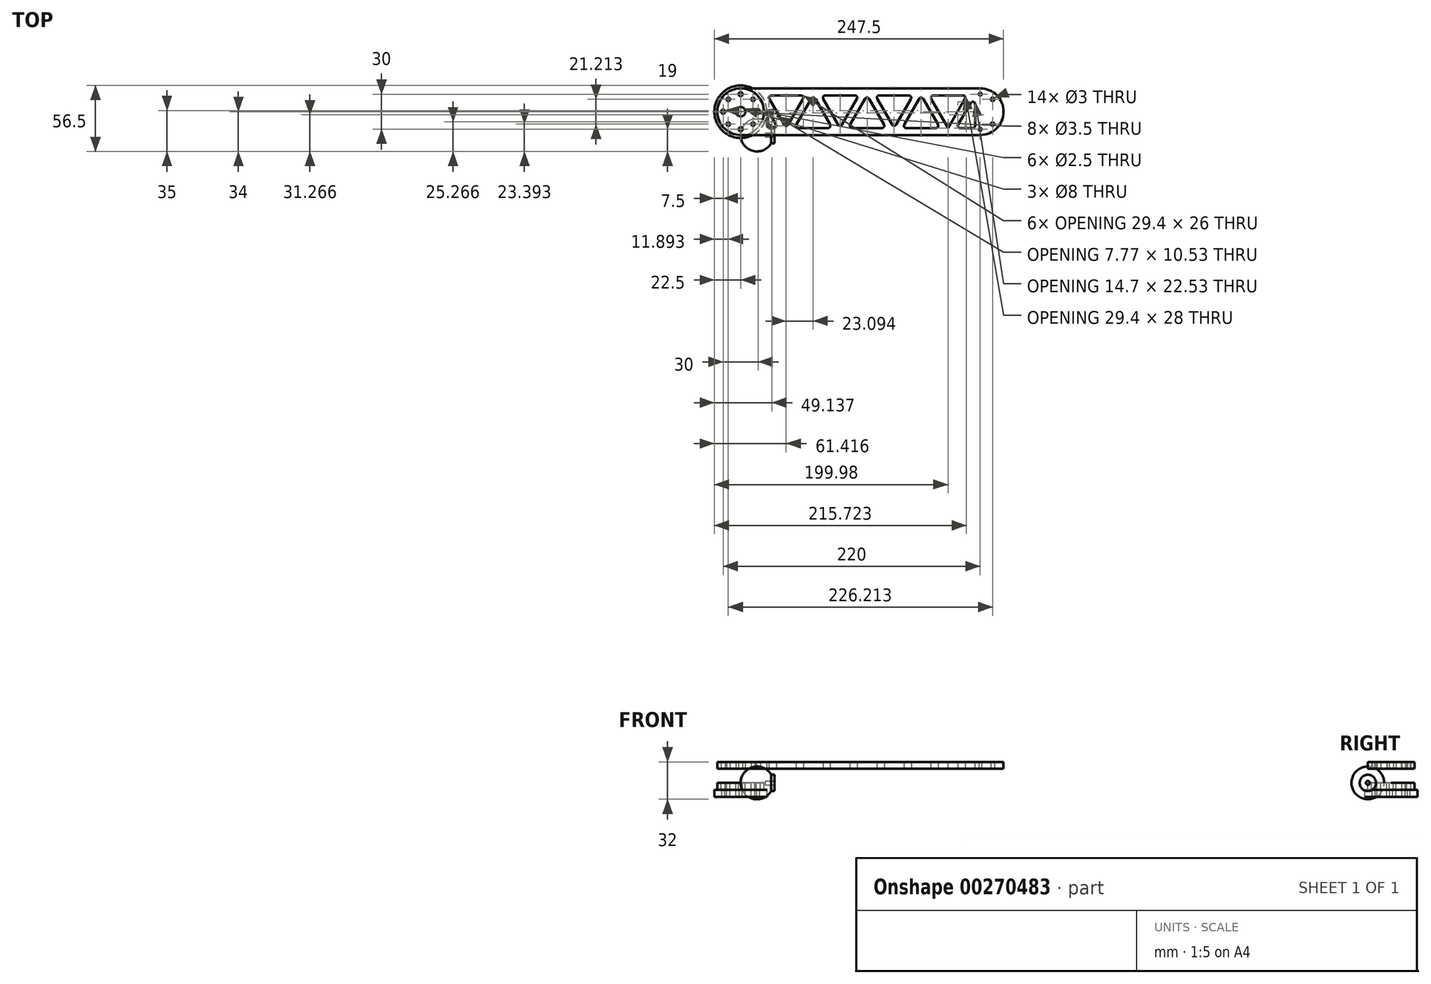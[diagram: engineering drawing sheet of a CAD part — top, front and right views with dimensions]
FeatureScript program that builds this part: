
annotation { "Feature Type Name" : "Feature", "Feature Type Description" : "" }
export const myFeature = defineFeature(function(context is Context, id is Id, definition is map)
    precondition{}
    {
        {
            var Q0;
            Q0=qCreatedBy(makeId("Top.planeOp"),FACE);
            var sketch = newSketch(context, id + "F0", { "sketchPlane" : qUnion([Q0])});
            skLineSegment(sketch, "E0.bottom", {"start": v(0, 0) * mm, "end": v(205, 0) * mm});
            skLineSegment(sketch, "E0.top", {"start": v(0, 40) * mm, "end": v(205, 40) * mm});
            skArc(sketch, "E1", {"start": v(205, 40) * mm, "mid": v(225, 20) * mm, "end": v(205, 0) * mm});
            skArc(sketch, "E2", {"start": v(0, 40) * mm, "mid": v(-20, 20) * mm, "end": v(0, 0) * mm});
            skCircle(sketch, "E3", {"center": v(0, 20) * mm, "radius": 15 * mm, "construction": true});
            skCircle(sketch, "E4", {"center": v(0, 35) * mm, "radius": 1.75 * mm});
            skCircle(sketch, "E5.1.0", {"center": v(-15, 20) * mm, "radius": 1.75 * mm});
            skCircle(sketch, "E5.2.0", {"center": v(0, 5) * mm, "radius": 1.75 * mm});
            skCircle(sketch, "E5.3.0", {"center": v(15, 20) * mm, "radius": 1.75 * mm});
            skLineSegment(sketch, "E6", {"start": v(0, 20) * mm, "end": v(10.6, 30.6) * mm});
            skCircle(sketch, "E7", {"center": v(10.6, 30.6) * mm, "radius": 1.5 * mm});
            skCircle(sketch, "E8.1.0", {"center": v(-10.6, 30.6) * mm, "radius": 1.5 * mm});
            skCircle(sketch, "E8.2.0", {"center": v(-10.6, 9.4) * mm, "radius": 1.5 * mm});
            skCircle(sketch, "E8.3.0", {"center": v(10.6, 9.4) * mm, "radius": 1.5 * mm});
            skCircle(sketch, "E9", {"center": v(0, 20) * mm, "radius": 4 * mm});
            skLineSegment(sketch, "E10", {"start": v(102.5, 40) * mm, "end": v(102.5, 0) * mm, "construction": true});
            skCircle(sketch, "E11.MirrorC", {"center": v(215.6, 30.6) * mm, "radius": 1.5 * mm});
            skCircle(sketch, "E12.MirrorC", {"center": v(215.6, 9.4) * mm, "radius": 1.5 * mm});
            skLineSegment(sketch, "E13.MirrorCS", {"start": v(205, 20) * mm, "end": v(194.4, 30.6) * mm});
            skCircle(sketch, "E14.MirrorC", {"center": v(205, 20) * mm, "radius": 15 * mm, "construction": true});
            skCircle(sketch, "E15", {"center": v(205, 5) * mm, "radius": 1.25 * mm});
            skCircle(sketch, "E16", {"center": v(205, 35) * mm, "radius": 1.25 * mm});
            skSolve(sketch);
        }
        {
            var Q0;
            Q0=qSketchRegion(id+"F0",true);
            extrude(context, id + "F1", {"entities" : qUnion([Q0]), "depth" : 6 * mm});
        }
        {
            var Q0;
            Q0=makeQuery(id+"F1.opExtrude","CAP_FACE",FACE,{"disambiguationData":[OSD([sQuery(id+"F0.wireOp",EDGE,"E0.bottom"),sQuery(id+"F0.wireOp",EDGE,"E0.top"),sQuery(id+"F0.wireOp",EDGE,"E2"),sQuery(id+"F0.wireOp",EDGE,"E4"),sQuery(id+"F0.wireOp",EDGE,"E5.1.0"),sQuery(id+"F0.wireOp",EDGE,"E5.2.0"),sQuery(id+"F0.wireOp",EDGE,"E5.3.0"),sQuery(id+"F0.wireOp",EDGE,"E7"),sQuery(id+"F0.wireOp",EDGE,"E8.1.0"),sQuery(id+"F0.wireOp",EDGE,"E8.2.0"),sQuery(id+"F0.wireOp",EDGE,"E8.3.0"),sQuery(id+"F0.wireOp",EDGE,"E9"),sQuery(id+"F0.wireOp",EDGE,"41661442-f439-4f29-86a3-6f938a79d0c80.MirrorC"),sQuery(id+"F0.wireOp",EDGE,"E11.MirrorC"),sQuery(id+"F0.wireOp",EDGE,"E12.MirrorC"),sQuery(id+"F0.wireOp",EDGE,"E1"),sQuery(id+"F0.wireOp",EDGE,"41661442-f439-4f29-86a3-6f938a79d0c812.MirrorC")])],"isStart":false});
            var sketch = newSketch(context, id + "F2", { "sketchPlane" : qUnion([Q0])});
            skLineSegment(sketch, "E17.left", {"start": v(22.75, 34) * mm, "end": v(22.75, 6) * mm, "construction": true});
            skLineSegment(sketch, "E17.right", {"start": v(200.57, 33.96) * mm, "end": v(200.57, 6) * mm, "construction": true});
            skLineSegment(sketch, "E18", {"start": v(22.75, 34) * mm, "end": v(55.08, 34) * mm});
            skLineSegment(sketch, "E19", {"start": v(55.08, 34) * mm, "end": v(38.92, 6) * mm});
            skLineSegment(sketch, "E20", {"start": v(38.92, 6) * mm, "end": v(22.75, 34) * mm});
            skLineSegment(sketch, "E21", {"start": v(45.84, 6) * mm, "end": v(62, 34) * mm});
            skLineSegment(sketch, "E22", {"start": v(62, 34) * mm, "end": v(78.18, 6) * mm});
            skLineSegment(sketch, "E23", {"start": v(78.18, 6) * mm, "end": v(45.84, 6) * mm});
            skLineSegment(sketch, "E24", {"start": v(22.75, 6) * mm, "end": v(200.57, 6) * mm, "construction": true});
            skLineSegment(sketch, "E25", {"start": v(55.08, 34) * mm, "end": v(22.75, 34) * mm, "construction": true});
            skPoint(sketch, "E26.visualSharp", {"position": v(22.75, 34) * mm});
            skPoint(sketch, "E27.visualSharp", {"position": v(38.92, 6) * mm});
            skLineSegment(sketch, "E28.1.0.0", {"start": v(101.27, 34) * mm, "end": v(85.1, 6) * mm});
            skPoint(sketch, "E28.1.0.1", {"position": v(68.94, 34) * mm});
            skLineSegment(sketch, "E28.1.0.2", {"start": v(85.1, 6) * mm, "end": v(68.94, 34) * mm});
            skLineSegment(sketch, "E28.1.0.3", {"start": v(108.2, 34) * mm, "end": v(124.36, 6) * mm});
            skLineSegment(sketch, "E28.1.0.4", {"start": v(92.03, 6) * mm, "end": v(108.2, 34) * mm});
            skPoint(sketch, "E28.1.0.5", {"position": v(85.1, 6) * mm});
            skLineSegment(sketch, "E28.1.0.6", {"start": v(101.27, 34) * mm, "end": v(68.94, 34) * mm, "construction": true});
            skLineSegment(sketch, "E28.1.0.7", {"start": v(124.36, 6) * mm, "end": v(92.03, 6) * mm});
            skLineSegment(sketch, "E28.1.0.8", {"start": v(68.94, 34) * mm, "end": v(101.27, 34) * mm});
            skLineSegment(sketch, "E28.2.0.0", {"start": v(147.46, 34) * mm, "end": v(131.3, 6) * mm});
            skPoint(sketch, "E28.2.0.1", {"position": v(115.13, 34) * mm});
            skLineSegment(sketch, "E28.2.0.2", {"start": v(131.3, 6) * mm, "end": v(115.13, 34) * mm});
            skLineSegment(sketch, "E28.2.0.3", {"start": v(154.39, 34) * mm, "end": v(170.55, 6) * mm});
            skLineSegment(sketch, "E28.2.0.4", {"start": v(138.22, 6) * mm, "end": v(154.39, 34) * mm});
            skPoint(sketch, "E28.2.0.5", {"position": v(131.3, 6) * mm});
            skLineSegment(sketch, "E28.2.0.6", {"start": v(147.46, 34) * mm, "end": v(115.13, 34) * mm, "construction": true});
            skLineSegment(sketch, "E28.2.0.7", {"start": v(170.55, 6) * mm, "end": v(138.22, 6) * mm});
            skLineSegment(sketch, "E28.2.0.8", {"start": v(115.13, 34) * mm, "end": v(147.46, 34) * mm});
            skLineSegment(sketch, "E28.direction1", {"start": v(38.92, 6) * mm, "end": v(85.1, 6) * mm, "construction": true});
            skLineSegment(sketch, "E29.0.3.0", {"start": v(193.65, 34) * mm, "end": v(177.48, 6) * mm});
            skPoint(sketch, "E29.3.3.0", {"position": v(161.31, 34) * mm});
            skLineSegment(sketch, "E29.4.3.0", {"start": v(177.48, 6) * mm, "end": v(161.31, 34) * mm});
            skPoint(sketch, "E29.13.3.0", {"position": v(177.48, 6) * mm});
            skLineSegment(sketch, "E29.14.3.0", {"start": v(193.65, 34) * mm, "end": v(161.31, 34) * mm, "construction": true});
            skLineSegment(sketch, "E29.20.3.0", {"start": v(161.31, 34) * mm, "end": v(193.65, 34) * mm});
            skLineSegment(sketch, "E30", {"start": v(200.57, 34) * mm, "end": v(184.4, 6) * mm});
            skLineSegment(sketch, "E31", {"start": v(184.4, 6) * mm, "end": v(200.57, 6) * mm});
            skLineSegment(sketch, "E32", {"start": v(200.57, 6) * mm, "end": v(200.57, 34) * mm});
            skLineSegment(sketch, "E33", {"start": v(22.75, 6) * mm, "end": v(31.99, 6) * mm});
            skLineSegment(sketch, "E34", {"start": v(31.99, 6) * mm, "end": v(22.75, 22) * mm});
            skLineSegment(sketch, "E35", {"start": v(22.75, 22) * mm, "end": v(22.75, 6) * mm});
            skSolve(sketch);
        }
        {
            var Q0;
            Q0=qSketchRegion(id+"F2",true);
            extrude(context, id + "F3", {"entities" : qUnion([Q0]), "operationType" : NewBodyOperationType.REMOVE, "endBound" : BoundingType.THROUGH_ALL, "oppositeDirection" : true, "depth" : 25 * mm});
        }
        {
            var Q0;
            Q0=makeQuery(id+"F3.boolean.opBoolean","COPY",EDGE,{"derivedFrom":makeQuery(id+"F3.opExtrude","SWEPT_EDGE",EDGE,{"disambiguationData":[OSD([sQuery(id+"F2.wireOp",EDGE,"E18"),sQuery(id+"F2.wireOp",EDGE,"E20")])]})});
            var Q1;
            Q1=makeQuery(id+"F3.boolean.opBoolean","COPY",EDGE,{"derivedFrom":makeQuery(id+"F3.opExtrude","SWEPT_EDGE",EDGE,{"disambiguationData":[OSD([sQuery(id+"F2.wireOp",EDGE,"E18"),sQuery(id+"F2.wireOp",EDGE,"E19")])]})});
            var Q2;
            Q2=makeQuery(id+"F3.boolean.opBoolean","COPY",EDGE,{"derivedFrom":makeQuery(id+"F3.opExtrude","SWEPT_EDGE",EDGE,{"disambiguationData":[OSD([sQuery(id+"F2.wireOp",EDGE,"E19"),sQuery(id+"F2.wireOp",EDGE,"E20")])]})});
            var Q3;
            Q3=makeQuery(id+"F3.boolean.opBoolean","COPY",EDGE,{"derivedFrom":makeQuery(id+"F3.opExtrude","SWEPT_EDGE",EDGE,{"disambiguationData":[OSD([sQuery(id+"F2.wireOp",EDGE,"E21"),sQuery(id+"F2.wireOp",EDGE,"E23")])]})});
            var Q4;
            Q4=makeQuery(id+"F3.boolean.opBoolean","COPY",EDGE,{"derivedFrom":makeQuery(id+"F3.opExtrude","SWEPT_EDGE",EDGE,{"disambiguationData":[OSD([sQuery(id+"F2.wireOp",EDGE,"E21"),sQuery(id+"F2.wireOp",EDGE,"E22")])]})});
            var Q5;
            Q5=makeQuery(id+"F3.boolean.opBoolean","COPY",EDGE,{"derivedFrom":makeQuery(id+"F3.opExtrude","SWEPT_EDGE",EDGE,{"disambiguationData":[OSD([sQuery(id+"F2.wireOp",EDGE,"E22"),sQuery(id+"F2.wireOp",EDGE,"E23")])]})});
            var Q6;
            Q6=makeQuery(id+"F3.boolean.opBoolean","COPY",EDGE,{"derivedFrom":makeQuery(id+"F3.opExtrude","SWEPT_EDGE",EDGE,{"disambiguationData":[OSD([sQuery(id+"F2.wireOp",EDGE,"E34"),sQuery(id+"F2.wireOp",EDGE,"E35")])]})});
            var Q7;
            Q7=makeQuery(id+"F3.boolean.opBoolean","COPY",EDGE,{"derivedFrom":makeQuery(id+"F3.opExtrude","SWEPT_EDGE",EDGE,{"disambiguationData":[OSD([sQuery(id+"F2.wireOp",EDGE,"E33"),sQuery(id+"F2.wireOp",EDGE,"E35")])]})});
            var Q8;
            Q8=makeQuery(id+"F3.boolean.opBoolean","COPY",EDGE,{"derivedFrom":makeQuery(id+"F3.opExtrude","SWEPT_EDGE",EDGE,{"disambiguationData":[OSD([sQuery(id+"F2.wireOp",EDGE,"E33"),sQuery(id+"F2.wireOp",EDGE,"E34")])]})});
            var Q9;
            Q9=makeQuery(id+"F3.boolean.opBoolean","COPY",EDGE,{"derivedFrom":makeQuery(id+"F3.opExtrude","SWEPT_EDGE",EDGE,{"disambiguationData":[OSD([sQuery(id+"F2.wireOp",EDGE,"E28.1.0.2"),sQuery(id+"F2.wireOp",EDGE,"E28.1.0.8")])]})});
            var Q10;
            Q10=makeQuery(id+"F3.boolean.opBoolean","COPY",EDGE,{"derivedFrom":makeQuery(id+"F3.opExtrude","SWEPT_EDGE",EDGE,{"disambiguationData":[OSD([sQuery(id+"F2.wireOp",EDGE,"E28.1.0.0"),sQuery(id+"F2.wireOp",EDGE,"E28.1.0.8")])]})});
            var Q11;
            Q11=makeQuery(id+"F3.boolean.opBoolean","COPY",EDGE,{"derivedFrom":makeQuery(id+"F3.opExtrude","SWEPT_EDGE",EDGE,{"disambiguationData":[OSD([sQuery(id+"F2.wireOp",EDGE,"E28.1.0.0"),sQuery(id+"F2.wireOp",EDGE,"E28.1.0.2")])]})});
            var Q12;
            Q12=makeQuery(id+"F3.boolean.opBoolean","COPY",EDGE,{"derivedFrom":makeQuery(id+"F3.opExtrude","SWEPT_EDGE",EDGE,{"disambiguationData":[OSD([sQuery(id+"F2.wireOp",EDGE,"E28.1.0.4"),sQuery(id+"F2.wireOp",EDGE,"E28.1.0.7")])]})});
            var Q13;
            Q13=makeQuery(id+"F3.boolean.opBoolean","COPY",EDGE,{"derivedFrom":makeQuery(id+"F3.opExtrude","SWEPT_EDGE",EDGE,{"disambiguationData":[OSD([sQuery(id+"F2.wireOp",EDGE,"E28.1.0.3"),sQuery(id+"F2.wireOp",EDGE,"E28.1.0.4")])]})});
            var Q14;
            Q14=makeQuery(id+"F3.boolean.opBoolean","COPY",EDGE,{"derivedFrom":makeQuery(id+"F3.opExtrude","SWEPT_EDGE",EDGE,{"disambiguationData":[OSD([sQuery(id+"F2.wireOp",EDGE,"E28.1.0.3"),sQuery(id+"F2.wireOp",EDGE,"E28.1.0.7")])]})});
            var Q15;
            Q15=makeQuery(id+"F3.boolean.opBoolean","COPY",EDGE,{"derivedFrom":makeQuery(id+"F3.opExtrude","SWEPT_EDGE",EDGE,{"disambiguationData":[OSD([sQuery(id+"F2.wireOp",EDGE,"E28.2.0.2"),sQuery(id+"F2.wireOp",EDGE,"E28.2.0.8")])]})});
            var Q16;
            Q16=makeQuery(id+"F3.boolean.opBoolean","COPY",EDGE,{"derivedFrom":makeQuery(id+"F3.opExtrude","SWEPT_EDGE",EDGE,{"disambiguationData":[OSD([sQuery(id+"F2.wireOp",EDGE,"E29.4.3.0"),sQuery(id+"F2.wireOp",EDGE,"E29.20.3.0")])]})});
            var Q17;
            Q17=makeQuery(id+"F3.boolean.opBoolean","COPY",EDGE,{"derivedFrom":makeQuery(id+"F3.opExtrude","SWEPT_EDGE",EDGE,{"disambiguationData":[OSD([sQuery(id+"F2.wireOp",EDGE,"E28.2.0.0"),sQuery(id+"F2.wireOp",EDGE,"E28.2.0.8")])]})});
            var Q18;
            Q18=makeQuery(id+"F3.boolean.opBoolean","COPY",EDGE,{"derivedFrom":makeQuery(id+"F3.opExtrude","SWEPT_EDGE",EDGE,{"disambiguationData":[OSD([sQuery(id+"F2.wireOp",EDGE,"E29.0.3.0"),sQuery(id+"F2.wireOp",EDGE,"E29.20.3.0")])]})});
            var Q19;
            Q19=makeQuery(id+"F3.boolean.opBoolean","COPY",EDGE,{"derivedFrom":makeQuery(id+"F3.opExtrude","SWEPT_EDGE",EDGE,{"disambiguationData":[OSD([sQuery(id+"F2.wireOp",EDGE,"E28.2.0.0"),sQuery(id+"F2.wireOp",EDGE,"E28.2.0.2")])]})});
            var Q20;
            Q20=makeQuery(id+"F3.boolean.opBoolean","COPY",EDGE,{"derivedFrom":makeQuery(id+"F3.opExtrude","SWEPT_EDGE",EDGE,{"disambiguationData":[OSD([sQuery(id+"F2.wireOp",EDGE,"E28.2.0.3"),sQuery(id+"F2.wireOp",EDGE,"E28.2.0.4")])]})});
            var Q21;
            Q21=makeQuery(id+"F3.boolean.opBoolean","COPY",EDGE,{"derivedFrom":makeQuery(id+"F3.opExtrude","SWEPT_EDGE",EDGE,{"disambiguationData":[OSD([sQuery(id+"F2.wireOp",EDGE,"E28.2.0.3"),sQuery(id+"F2.wireOp",EDGE,"E28.2.0.7")])]})});
            var Q22;
            Q22=makeQuery(id+"F3.boolean.opBoolean","COPY",EDGE,{"derivedFrom":makeQuery(id+"F3.opExtrude","SWEPT_EDGE",EDGE,{"disambiguationData":[OSD([sQuery(id+"F2.wireOp",EDGE,"E28.2.0.4"),sQuery(id+"F2.wireOp",EDGE,"E28.2.0.7")])]})});
            var Q23;
            Q23=makeQuery(id+"F3.boolean.opBoolean","COPY",EDGE,{"derivedFrom":makeQuery(id+"F3.opExtrude","SWEPT_EDGE",EDGE,{"disambiguationData":[OSD([sQuery(id+"F2.wireOp",EDGE,"E31"),sQuery(id+"F2.wireOp",EDGE,"E32")])]})});
            var Q24;
            Q24=makeQuery(id+"F3.boolean.opBoolean","COPY",EDGE,{"derivedFrom":makeQuery(id+"F3.opExtrude","SWEPT_EDGE",EDGE,{"disambiguationData":[OSD([sQuery(id+"F2.wireOp",EDGE,"E30"),sQuery(id+"F2.wireOp",EDGE,"E31")])]})});
            var Q25;
            Q25=makeQuery(id+"F3.boolean.opBoolean","COPY",EDGE,{"derivedFrom":makeQuery(id+"F3.opExtrude","SWEPT_EDGE",EDGE,{"disambiguationData":[OSD([sQuery(id+"F2.wireOp",EDGE,"E30"),sQuery(id+"F2.wireOp",EDGE,"E32")])]})});
            fillet(context, id + "F4", {"entities" : qUnion([Q0, Q1, Q2, Q3, Q4, Q5, Q6, Q7, Q8, Q9, Q10, Q11, Q12, Q13, Q14, Q15, Q16, Q17, Q18, Q19, Q20, Q21, Q22, Q23, Q24, Q25]), "radius" : 2 * mm, "tangentPropagation" : true, "allowEdgeOverflow" : false});
        }
        {
            var Q0;
            Q0=qCreatedBy(makeId("Top.planeOp"),FACE);
            var sketch = newSketch(context, id + "F5", { "sketchPlane" : qUnion([Q0])});
            skLineSegment(sketch, "E36", {"start": v(29, 0) * mm, "end": v(29, 7) * mm});
            skLineSegment(sketch, "E37", {"start": v(29, 7) * mm, "end": v(26.12, 7) * mm});
            skArc(sketch, "E38", {"start": v(26.12, 7) * mm, "mid": v(10.38, 13.52) * mm, "end": v(0, 0) * mm});
            skLineSegment(sketch, "E39", {"start": v(29, 0) * mm, "end": v(0, 0) * mm});
            skSolve(sketch);
        }
        {
            var Q0;
            Q0=qSketchRegion(id+"F5",true);
            var Q1;
            Q1=sQuery(id+"F5.wireOp",EDGE,"E39");
            revolve(context, id + "F6", {"entities" : qUnion([Q0]), "axis" : qUnion([Q1]), "revolveType" : RevolveType.FULL});
        }
        {
            var Q0;
            Q0=makeQuery(id+"F1.opExtrude","SWEPT_BODY",BODY,{"disambiguationData":[OSD([sQuery(id+"F0.wireOp",EDGE,"E0.bottom"),sQuery(id+"F0.wireOp",EDGE,"E0.top"),sQuery(id+"F0.wireOp",EDGE,"E2"),sQuery(id+"F0.wireOp",EDGE,"E4"),sQuery(id+"F0.wireOp",EDGE,"E5.1.0"),sQuery(id+"F0.wireOp",EDGE,"E5.2.0"),sQuery(id+"F0.wireOp",EDGE,"E5.3.0"),sQuery(id+"F0.wireOp",EDGE,"E7"),sQuery(id+"F0.wireOp",EDGE,"E8.1.0"),sQuery(id+"F0.wireOp",EDGE,"E8.2.0"),sQuery(id+"F0.wireOp",EDGE,"E8.3.0"),sQuery(id+"F0.wireOp",EDGE,"E9"),sQuery(id+"F0.wireOp",EDGE,"41661442-f439-4f29-86a3-6f938a79d0c80.MirrorC"),sQuery(id+"F0.wireOp",EDGE,"E11.MirrorC"),sQuery(id+"F0.wireOp",EDGE,"E12.MirrorC"),sQuery(id+"F0.wireOp",EDGE,"E1"),sQuery(id+"F0.wireOp",EDGE,"41661442-f439-4f29-86a3-6f938a79d0c812.MirrorC")])]});
            transform(context, id + "F7", {"entities" : qUnion([Q0]), "transformType" : TransformType.TRANSLATION_3D, "dx" : 0 * mm, "dy" : 0 * mm, "dz" : 6 * mm, "makeCopy" : true});
        }
        {
            var Q0;
            Q0=makeQuery(id+"F7.opPattern","COPY",BODY,{"derivedFrom":makeQuery(id+"F1.opExtrude","SWEPT_BODY",BODY,{"disambiguationData":[OSD([sQuery(id+"F0.wireOp",EDGE,"E0.bottom"),sQuery(id+"F0.wireOp",EDGE,"E0.top"),sQuery(id+"F0.wireOp",EDGE,"E2"),sQuery(id+"F0.wireOp",EDGE,"E4"),sQuery(id+"F0.wireOp",EDGE,"E5.1.0"),sQuery(id+"F0.wireOp",EDGE,"E5.2.0"),sQuery(id+"F0.wireOp",EDGE,"E5.3.0"),sQuery(id+"F0.wireOp",EDGE,"E7"),sQuery(id+"F0.wireOp",EDGE,"E8.1.0"),sQuery(id+"F0.wireOp",EDGE,"E8.2.0"),sQuery(id+"F0.wireOp",EDGE,"E8.3.0"),sQuery(id+"F0.wireOp",EDGE,"E9"),sQuery(id+"F0.wireOp",EDGE,"41661442-f439-4f29-86a3-6f938a79d0c80.MirrorC"),sQuery(id+"F0.wireOp",EDGE,"E11.MirrorC"),sQuery(id+"F0.wireOp",EDGE,"E12.MirrorC"),sQuery(id+"F0.wireOp",EDGE,"E1"),sQuery(id+"F0.wireOp",EDGE,"41661442-f439-4f29-86a3-6f938a79d0c812.MirrorC")])]}),"instanceName":"1"});
            transform(context, id + "F8", {"entities" : qUnion([Q0]), "transformType" : TransformType.TRANSLATION_3D, "dx" : 0 * mm, "dy" : 0 * mm, "dz" : 6 * mm, "makeCopy" : true});
        }
        {
            var Q0;
            Q0=makeQuery(id+"F6.opRevolve","SWEPT_FACE",FACE,{"disambiguationData":[OSD([sQuery(id+"F5.wireOp",EDGE,"E36")])]});
            var sketch = newSketch(context, id + "F9", { "sketchPlane" : qUnion([Q0])});
            skCircle(sketch, "E40", {"center": v(0, 0) * mm, "radius": 1.7 * mm});
            skSolve(sketch);
        }
        {
            var Q0;
            Q0=qSketchRegion(id+"F9",true);
            extrude(context, id + "F10", {"entities" : qUnion([Q0]), "operationType" : NewBodyOperationType.REMOVE, "oppositeDirection" : true, "depth" : 7.7 * mm});
        }
        {
            var Q0;
            Q0=makeQuery(id+"F1.opExtrude","CAP_FACE",FACE,{"disambiguationData":[OSD([sQuery(id+"F0.wireOp",EDGE,"E0.bottom"),sQuery(id+"F0.wireOp",EDGE,"E0.top"),sQuery(id+"F0.wireOp",EDGE,"E2"),sQuery(id+"F0.wireOp",EDGE,"E4"),sQuery(id+"F0.wireOp",EDGE,"E5.1.0"),sQuery(id+"F0.wireOp",EDGE,"E5.2.0"),sQuery(id+"F0.wireOp",EDGE,"E5.3.0"),sQuery(id+"F0.wireOp",EDGE,"E7"),sQuery(id+"F0.wireOp",EDGE,"E8.1.0"),sQuery(id+"F0.wireOp",EDGE,"E8.2.0"),sQuery(id+"F0.wireOp",EDGE,"E8.3.0"),sQuery(id+"F0.wireOp",EDGE,"E9"),sQuery(id+"F0.wireOp",EDGE,"E11.MirrorC"),sQuery(id+"F0.wireOp",EDGE,"E12.MirrorC"),sQuery(id+"F0.wireOp",EDGE,"E1"),sQuery(id+"F0.wireOp",EDGE,"E15"),sQuery(id+"F0.wireOp",EDGE,"E16")])],"isStart":true});
            var sketch = newSketch(context, id + "F11", { "sketchPlane" : qUnion([Q0])});
            skCircle(sketch, "E41", {"center": v(0, -20) * mm, "radius": 20 * mm});
            skCircle(sketch, "E42", {"center": v(0, -20) * mm, "radius": 4 * mm});
            skCircle(sketch, "E43", {"center": v(15, -20) * mm, "radius": 1.75 * mm});
            skCircle(sketch, "E44", {"center": v(10.6, -9.4) * mm, "radius": 1.5 * mm});
            skCircle(sketch, "E45", {"center": v(0, -5) * mm, "radius": 1.75 * mm});
            skCircle(sketch, "E46", {"center": v(-10.6, -9.4) * mm, "radius": 1.5 * mm});
            skCircle(sketch, "E47", {"center": v(-15, -20) * mm, "radius": 1.75 * mm});
            skCircle(sketch, "E48", {"center": v(-10.6, -30.6) * mm, "radius": 1.5 * mm});
            skCircle(sketch, "E49", {"center": v(0, -35) * mm, "radius": 1.75 * mm});
            skCircle(sketch, "E50", {"center": v(10.6, -30.6) * mm, "radius": 1.5 * mm});
            skSolve(sketch);
        }
        {
            var Q0;
            Q0=qSketchRegion(id+"F11",true);
            extrude(context, id + "F12", {"entities" : qUnion([Q0]), "depth" : 6 * mm});
        }
        {
            var Q0;
            Q0=makeQuery(id+"F12.opExtrude","CAP_FACE",FACE,{"disambiguationData":[OSD([sQuery(id+"F11.wireOp",EDGE,"E41"),sQuery(id+"F11.wireOp",EDGE,"E42"),sQuery(id+"F11.wireOp",EDGE,"E43"),sQuery(id+"F11.wireOp",EDGE,"E44"),sQuery(id+"F11.wireOp",EDGE,"E45"),sQuery(id+"F11.wireOp",EDGE,"E46"),sQuery(id+"F11.wireOp",EDGE,"E47"),sQuery(id+"F11.wireOp",EDGE,"E48"),sQuery(id+"F11.wireOp",EDGE,"E49"),sQuery(id+"F11.wireOp",EDGE,"E50")])],"isStart":false});
            var sketch = newSketch(context, id + "F13", { "sketchPlane" : qUnion([Q0])});
            skCircle(sketch, "E51", {"center": v(0, -20) * mm, "radius": 22.5 * mm});
            skCircle(sketch, "E52", {"center": v(0, -20) * mm, "radius": 4 * mm});
            skCircle(sketch, "E53", {"center": v(0, -5) * mm, "radius": 1.25 * mm});
            skCircle(sketch, "E54", {"center": v(10.6, -9.4) * mm, "radius": 1.5 * mm});
            skCircle(sketch, "E55", {"center": v(15, -20) * mm, "radius": 1.25 * mm});
            skCircle(sketch, "E56", {"center": v(10.6, -30.6) * mm, "radius": 1.5 * mm});
            skCircle(sketch, "E57", {"center": v(0, -35) * mm, "radius": 1.25 * mm});
            skCircle(sketch, "E58", {"center": v(-10.6, -30.6) * mm, "radius": 1.5 * mm});
            skCircle(sketch, "E59", {"center": v(-15, -20) * mm, "radius": 1.25 * mm});
            skCircle(sketch, "E60", {"center": v(-10.6, -9.4) * mm, "radius": 1.5 * mm});
            skSolve(sketch);
        }
        {
            var Q0;
            Q0 = qSketchRegion(id + "F13", true);
            extrude(context, id + "F14", {"entities" : qUnion([Q0]), "depth" : 6 * mm});
        }
        {
            var Q0;
            Q0=makeQuery(id+"F7.opPattern","COPY",BODY,{"derivedFrom":makeQuery(id+"F1.opExtrude","SWEPT_BODY",BODY,{"disambiguationData":[OSD([sQuery(id+"F0.wireOp",EDGE,"E0.bottom"),sQuery(id+"F0.wireOp",EDGE,"E0.top"),sQuery(id+"F0.wireOp",EDGE,"E2"),sQuery(id+"F0.wireOp",EDGE,"E4"),sQuery(id+"F0.wireOp",EDGE,"E5.1.0"),sQuery(id+"F0.wireOp",EDGE,"E5.2.0"),sQuery(id+"F0.wireOp",EDGE,"E5.3.0"),sQuery(id+"F0.wireOp",EDGE,"E7"),sQuery(id+"F0.wireOp",EDGE,"E8.1.0"),sQuery(id+"F0.wireOp",EDGE,"E8.2.0"),sQuery(id+"F0.wireOp",EDGE,"E8.3.0"),sQuery(id+"F0.wireOp",EDGE,"E9"),sQuery(id+"F0.wireOp",EDGE,"E11.MirrorC"),sQuery(id+"F0.wireOp",EDGE,"E12.MirrorC"),sQuery(id+"F0.wireOp",EDGE,"E1"),sQuery(id+"F0.wireOp",EDGE,"E15"),sQuery(id+"F0.wireOp",EDGE,"E16")])]}),"instanceName":"1"});
            deleteBodies(context, id + "F15", {"entities" : qUnion([Q0])});
        }
        {
            var Q0;
            Q0=makeQuery(id+"F1.opExtrude","SWEPT_BODY",BODY,{"disambiguationData":[OSD([sQuery(id+"F0.wireOp",EDGE,"E0.bottom"),sQuery(id+"F0.wireOp",EDGE,"E0.top"),sQuery(id+"F0.wireOp",EDGE,"E2"),sQuery(id+"F0.wireOp",EDGE,"E4"),sQuery(id+"F0.wireOp",EDGE,"E5.1.0"),sQuery(id+"F0.wireOp",EDGE,"E5.2.0"),sQuery(id+"F0.wireOp",EDGE,"E5.3.0"),sQuery(id+"F0.wireOp",EDGE,"E7"),sQuery(id+"F0.wireOp",EDGE,"E8.1.0"),sQuery(id+"F0.wireOp",EDGE,"E8.2.0"),sQuery(id+"F0.wireOp",EDGE,"E8.3.0"),sQuery(id+"F0.wireOp",EDGE,"E9"),sQuery(id+"F0.wireOp",EDGE,"E11.MirrorC"),sQuery(id+"F0.wireOp",EDGE,"E12.MirrorC"),sQuery(id+"F0.wireOp",EDGE,"E1"),sQuery(id+"F0.wireOp",EDGE,"E15"),sQuery(id+"F0.wireOp",EDGE,"E16")])]});
            deleteBodies(context, id + "F16", {"entities" : qUnion([Q0])});
        }
    });
